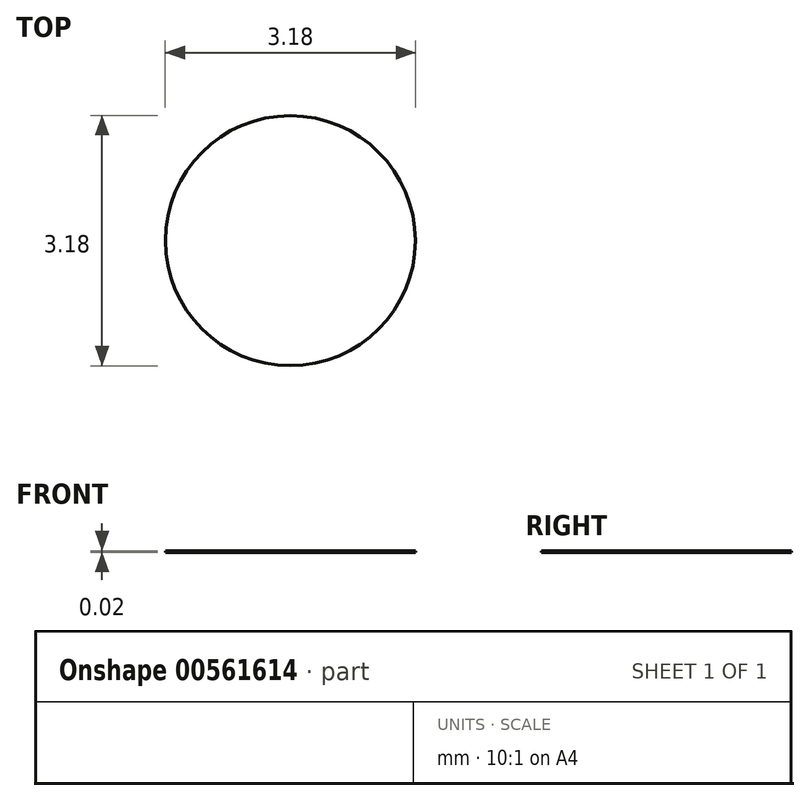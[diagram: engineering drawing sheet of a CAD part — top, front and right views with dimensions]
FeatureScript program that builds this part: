
annotation { "Feature Type Name" : "Feature", "Feature Type Description" : "" }
export const myFeature = defineFeature(function(context is Context, id is Id, definition is map)
    precondition{}
    {
        {
            assignVariable(context, id + "F0", {"name" : "ligPostHeight", "anyValue" : 1 / 50.8 * mm});
        }
        {
            var Q0;
            Q0=qCreatedBy(makeId("Top.planeOp"),FACE);
            var sketch = newSketch(context, id + "F1", { "sketchPlane" : qUnion([Q0])});
            skCircle(sketch, "E0", {"center": v(0, 0) * mm, "radius": 1.59 * mm});
            skSolve(sketch);
        }
        {
            var Q0;
            Q0 = qSketchRegion(id + "F1", true);
            extrude(context, id + "F2", {"entities" : qUnion([Q0]), "depth" : getVariable(context, 'ligPostHeight'), "offsetDistance" : 25.4 * mm});
        }
        {
            var Q0;
            Q0=qCreatedBy(makeId("Front.planeOp"),FACE);
            var sketch = newSketch(context, id + "F3", { "sketchPlane" : qUnion([Q0])});
            skCircle(sketch, "E1", {"center": v(0, 1.9) * mm, "radius": 0.8 * mm});
            skCircle(sketch, "E2", {"center": v(0, 4.76) * mm, "radius": 0.8 * mm});
            skSolve(sketch);
        }
        {
            var Q0;
            Q0 = qSketchRegion(id + "F3", true);
            extrude(context, id + "F4", {"entities" : qUnion([Q0]), "operationType" : NewBodyOperationType.REMOVE, "endBound" : BoundingType.SYMMETRIC, "oppositeDirection" : true, "depth" : 25.4 * mm, "offsetDistance" : 25.4 * mm});
        }
    });
